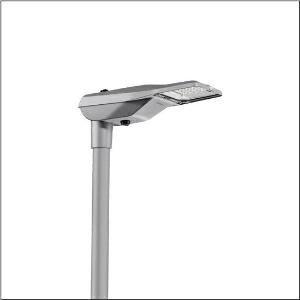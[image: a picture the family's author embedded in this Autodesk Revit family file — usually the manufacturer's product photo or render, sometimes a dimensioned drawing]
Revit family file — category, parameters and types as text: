
# Revit family: streetlight_sl_21_iq_micro___st0_8a_5xe1c31y08db_8273
name_source: partatom
category: Lighting Fixtures
units: mm (PartAtom-declared; Revit-internal decimal feet)

## family parameters
Cut with Voids When Loaded = No
Host = Face
Light Source = No
Part Type = Normal
Room Calculation Point = No
Round Connector Dimension = Use Diameter
Shared = No

## types (1)
- --- (1 x LED, 5110 lm, 39.1 W, 3000K)
    Apparent Load = 39 VA
    CIE Flux Codes = 38 75 97 100 100
    Color Rendering = 70
    Color Temperature = 3000K
    Default Elevation = 1800 mm
    Description = Streetlight SL 21 iQ micro, mast luminaire, primary light control with lens, of PMMA, primary optical cover: cover, of toughened safety glass, transparent, light distribution: ST0.8a, light emission: direct distribution, primary light characteristic: asymmetric, installation type: post-top, side-entry, LED, High Power LED, rated luminous flux: 5.110lm, luminous efficacy: 131lm/W, light colour: 730, colour temperature: 3000K, control: pre-setting: logarithmic dimming characteristic, Street-Remote, Auto-Match, Temp-Guard, Lumen-Switch, Night-Set, Smart-Wire, Light-Fading, Desk-Remote (wireless, voltage-free reading and setting of iQ features in the workshop via application-optimized NFC function/RFID function), optimised constant luminous flux control (CLO 2.0), mains connection: 220..240V, AC, 50/60Hz, start of lifetime: 39W, end of service life: 41W, reduction: 17W, luminaire housing, of diecast aluminium, powder-coated, Siteco® metallic grey (DB 702S), corrosivity category C5 mid according to DIN EN ISO 12944, please order mast flange separately, inclination adjustable: 0°, 5°, 10°, 15°, sealing non-destructively replaceable, multi-level sealing system, length: 528mm, width: 235mm, height: 110mm, mast flange for spigot size: 42mm (side-entry): 5XC10008XM4, 60/48mm (side-entry/post-top): 5XC10108XM2, 76/60mm (side-entry/post-top): 5XC10108XM1, Smart Interface below and above, protection rating (complete): IP66, insulation class (complete): insulation class II (safety insulation), certification: CE, ENEC, ENEC+, VDE, impact resistance: IK09, permissible operating ambient temperature for outdoor applications: -40..+50°C, standard-compliant lighting for roads and squares, packaging unit: 1 piece

Light Distribution: ST0.8a
    Height = 110 mm
    Lamp = 1 x LED
    Lamp Light Flux = 5110 lm
    Lamp Power = 39.1 W
    Lamp count = 1
    Length = 528 mm
    Luminous efficacy = 131 lm/W
    Manufacturer = Siteco
    ModVariant = No
    Model = 5XE1C31Y08DB
    Number of Poles = 1
    OnlyDefault = Yes
    Power Factor = 1
    Product Name = Streetlight SL 21 iQ micro | ST0.8a
    Product group = mast luminaire | pylon top
    ProductGroupID = 6100
    Protection Class = Protection class II
    Protection Degree = IP 66
    RLX_Detail_Level = 1
    RLX_Emergency_Light_Flux = 0 lm
    RLX_Emergency_Type = 0
    RLX_Emergency_Type_DB = No
    RlxData = <blob elided: 98765 chars, md5=70e20a03>
    Socket = socket
    Standby Power = 0 W
    System Light Flux = 5110 lm
    System Power = 39 W
    Type Comments = factory setting: luminous flux: 100 % | dim-lin: 254 | 765 mA
    Type Image = l_1007239.jpg
    URL = http://relux.com
    VarID = @adj_082233
    Voltage = 0 V
    Weight = 0.00 kg
    Width = 235 mm

## geometry (parser evidence)
native form markers: Blend x4, Sweep x11
no freeform markers — native parametric forms only
